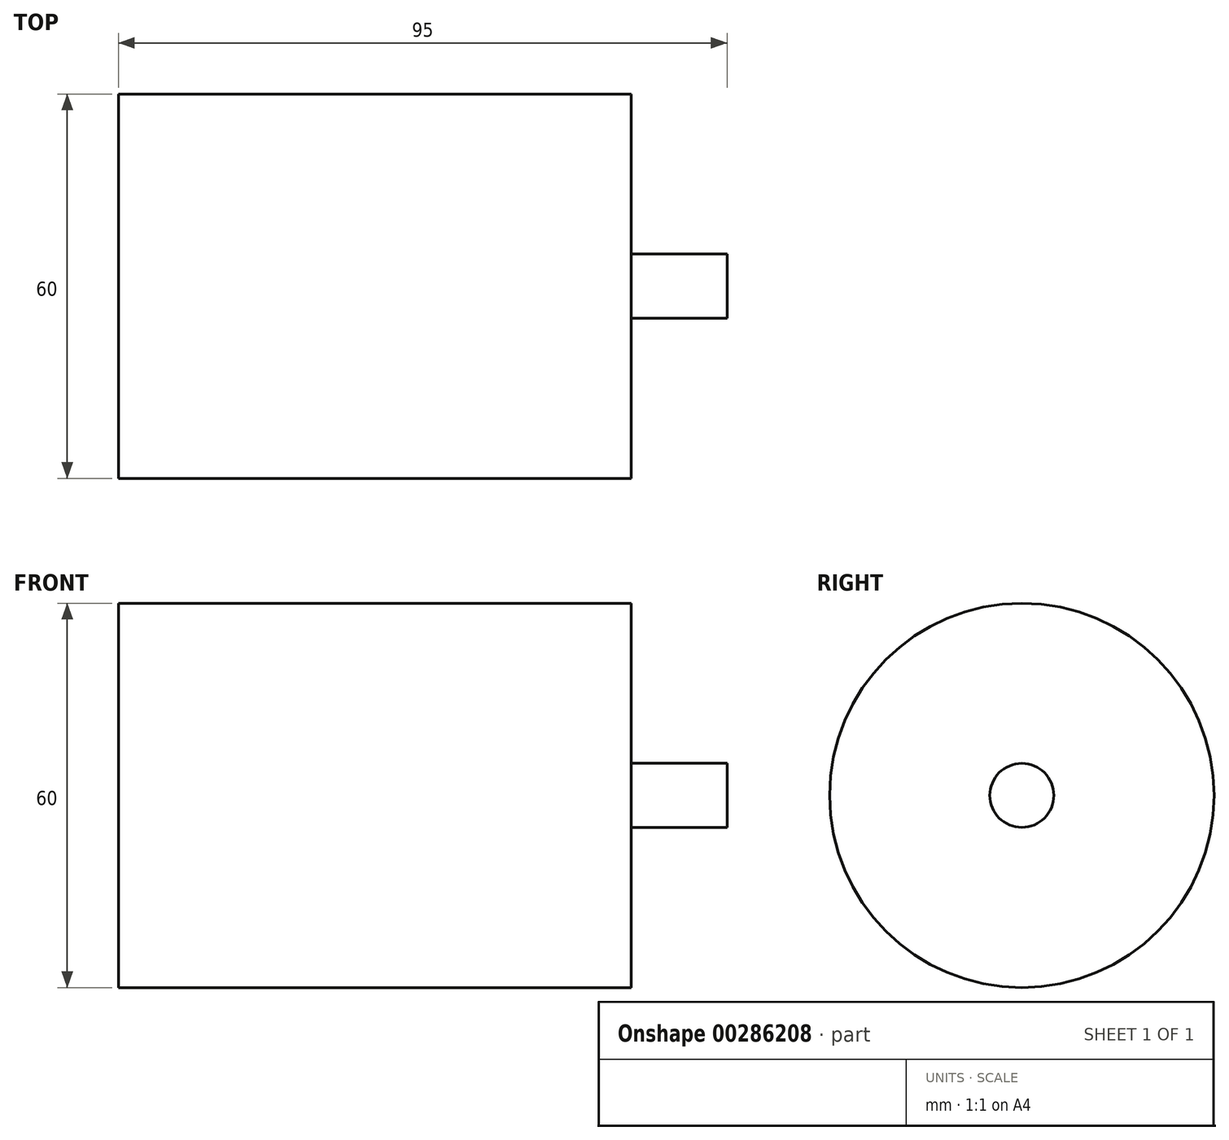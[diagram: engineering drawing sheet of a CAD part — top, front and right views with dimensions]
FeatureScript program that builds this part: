
annotation { "Feature Type Name" : "Feature", "Feature Type Description" : "" }
export const myFeature = defineFeature(function(context is Context, id is Id, definition is map)
    precondition{}
    {
        {
            var Q0;
            Q0=qCreatedBy(makeId("Front.planeOp"),FACE);
            var sketch = newSketch(context, id + "F0", { "sketchPlane" : qUnion([Q0])});
            skLineSegment(sketch, "E0", {"start": v(0, 0) * mm, "end": v(0, 30) * mm});
            skLineSegment(sketch, "E1", {"start": v(0, 30) * mm, "end": v(80, 30) * mm});
            skLineSegment(sketch, "E2", {"start": v(80, 30) * mm, "end": v(80, 5) * mm});
            skLineSegment(sketch, "E3", {"start": v(80, 5) * mm, "end": v(95, 5) * mm});
            skLineSegment(sketch, "E4", {"start": v(95, 5) * mm, "end": v(95, 0) * mm});
            skLineSegment(sketch, "E5", {"start": v(95, 0) * mm, "end": v(0, 0) * mm});
            skLineSegment(sketch, "E6", {"start": v(-67.91, 0) * mm, "end": v(57.57, 0) * mm, "construction": true});
            skSolve(sketch);
        }
        {
            var Q0;
            Q0=qSketchRegion(id+"F0",true);
            var Q1;
            Q1=sQuery(id+"F0.wireOp",EDGE,"E6");
            revolve(context, id + "F1", {"entities" : qUnion([Q0]), "axis" : qUnion([Q1]), "revolveType" : RevolveType.FULL});
        }
    });
